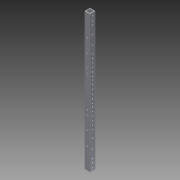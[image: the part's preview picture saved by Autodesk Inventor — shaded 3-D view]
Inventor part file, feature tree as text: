
AUTODESK INVENTOR PART (.ipt)
format: ipt  version: 2013 (Build 170138000, 138)  size: 232,960 bytes
history: native  units: in
note: dims shown in document units (in); Inventor stores cm internally (conversion verified against a paired STEP export)
features: reference x7, extrude x4, sketch x4
ambient origin geometry x8: Origin, YZ Plane, XZ Plane, XY Plane, X Axis, Y Axis, Z Axis, Center Point
bodies: Solid1 (feature_tree)
feature tree (15):
  extrude  "Extrusion1"  Depth=1.0in
  extrude  "Extrusion2"  Depth=26.0in TaperAngle=0.0deg
  extrude  "Extrusion3"  Depth=1.75in
  extrude  "Extrusion4"  Depth=1.75in
  sketch  "Sketch1"  dims[d0=1.0in d1=1.0in]
  sketch  "Sketch2"  dims[d2=0.125in d3=26.0in d4=0.0in]
  sketch  "Sketch3"  dims[d5=1.0in d6=0.0in d7=1.75in]
  reference  "Reference11"
  reference  "Reference12"
  reference  "Reference13"
  sketch  "Sketch4"  dims[d8=2.375in d9=1.75in d10=1.75in d11=0.26in d12=0.26in d13=0.26in d14=0.26in d15=0.26in d16=0.26in d17=0.26in d18=0.26in d19=1.0in d20=0.0in d21=2.375in d22=0.26in d23=0.26in d27=0.375in d28=0.375in d33=3.5in d34=0.26in d35=2.7559in d37=0.75in d38=0.3937in d40=1.0in d42=2.7559in d44=0.75in d45=0.3937in d47=1.0in d49=1.0in d50=0.0in d51=0.75in d52=0.75in d53=0.75in d54=0.75in]
  reference  "Reference15"
  reference  "Reference16"
  reference  "Reference17"
  reference  "Reference18"
